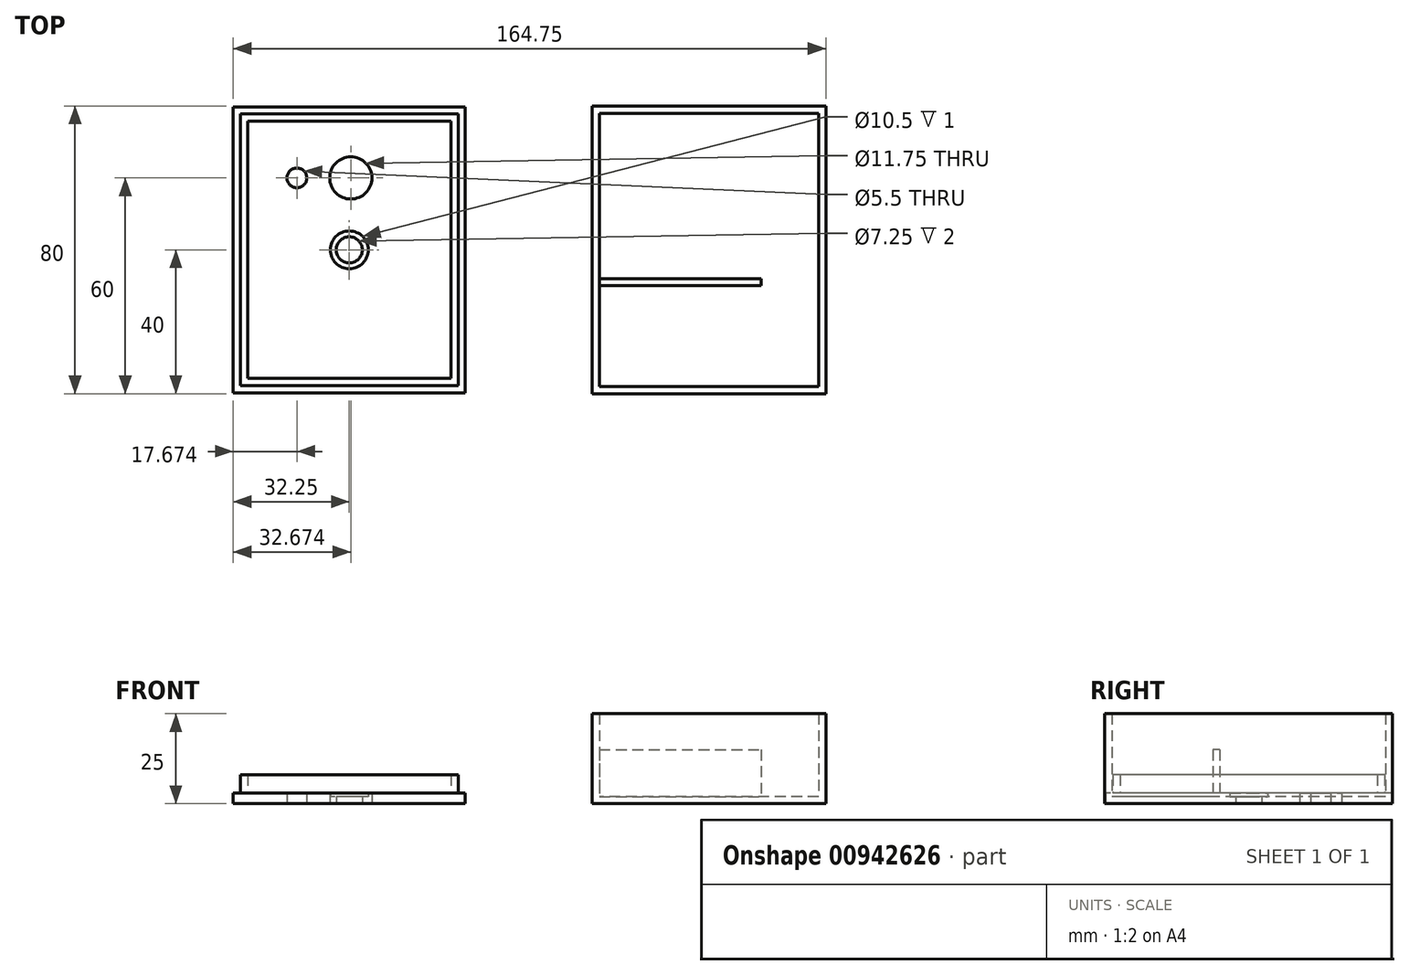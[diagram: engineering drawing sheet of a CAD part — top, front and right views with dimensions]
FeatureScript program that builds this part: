
annotation { "Feature Type Name" : "Feature", "Feature Type Description" : "" }
export const myFeature = defineFeature(function(context is Context, id is Id, definition is map)
    precondition{}
    {
        {
            var Q0;
            Q0=qCreatedBy(makeId("Top.planeOp"),FACE);
            var sketch = newSketch(context, id + "F0", { "sketchPlane" : qUnion([Q0])});
            skLineSegment(sketch, "E0.bottom", {"start": v(32.5, 40) * mm, "end": v(-32.5, 40) * mm});
            skLineSegment(sketch, "E0.top", {"start": v(32.5, -40) * mm, "end": v(-32.5, -40) * mm});
            skLineSegment(sketch, "E0.left", {"start": v(32.5, 40) * mm, "end": v(32.5, -40) * mm});
            skLineSegment(sketch, "E0.right", {"start": v(-32.5, 40) * mm, "end": v(-32.5, -40) * mm});
            skPoint(sketch, "E0.middle", {"position": v(0, 0) * mm});
            skLineSegment(sketch, "E1.0", {"start": v(30.5, 38) * mm, "end": v(-30.5, 38) * mm});
            skLineSegment(sketch, "E1.1", {"start": v(30.5, 38) * mm, "end": v(30.5, -38) * mm});
            skLineSegment(sketch, "E1.2", {"start": v(30.5, -38) * mm, "end": v(-30.5, -38) * mm});
            skLineSegment(sketch, "E1.3", {"start": v(-30.5, 38) * mm, "end": v(-30.5, -38) * mm});
            skLineSegment(sketch, "E2.bottom", {"start": v(-30.5, -8) * mm, "end": v(14.5, -8) * mm});
            skLineSegment(sketch, "E2.top", {"start": v(-30.5, -10) * mm, "end": v(14.5, -10) * mm});
            skLineSegment(sketch, "E2.left", {"start": v(-30.5, -8) * mm, "end": v(-30.5, -10) * mm});
            skLineSegment(sketch, "E2.right", {"start": v(14.5, -8) * mm, "end": v(14.5, -10) * mm});
            skLineSegment(sketch, "E3.bottom", {"start": v(-132.25, 39.75) * mm, "end": v(-67.75, 39.75) * mm});
            skLineSegment(sketch, "E3.top", {"start": v(-132.25, -39.75) * mm, "end": v(-67.75, -39.75) * mm});
            skLineSegment(sketch, "E3.left", {"start": v(-132.25, 39.75) * mm, "end": v(-132.25, -39.75) * mm});
            skLineSegment(sketch, "E3.right", {"start": v(-67.75, 39.75) * mm, "end": v(-67.75, -39.75) * mm});
            skPoint(sketch, "E3.middle", {"position": v(-100, 0) * mm});
            skLineSegment(sketch, "E4.0", {"start": v(-130.25, 37.75) * mm, "end": v(-69.75, 37.75) * mm});
            skLineSegment(sketch, "E4.1", {"start": v(-130.25, 37.75) * mm, "end": v(-130.25, -37.75) * mm});
            skLineSegment(sketch, "E4.2", {"start": v(-130.25, -37.75) * mm, "end": v(-69.75, -37.75) * mm});
            skLineSegment(sketch, "E4.3", {"start": v(-69.75, 37.75) * mm, "end": v(-69.75, -37.75) * mm});
            skLineSegment(sketch, "E5.0", {"start": v(-128.25, 35.75) * mm, "end": v(-71.75, 35.75) * mm});
            skLineSegment(sketch, "E5.1", {"start": v(-128.25, 35.75) * mm, "end": v(-128.25, -35.75) * mm});
            skLineSegment(sketch, "E5.2", {"start": v(-128.25, -35.75) * mm, "end": v(-71.75, -35.75) * mm});
            skLineSegment(sketch, "E5.3", {"start": v(-71.75, 35.75) * mm, "end": v(-71.75, -35.75) * mm});
            skCircle(sketch, "E6", {"center": v(-99.58, 20) * mm, "radius": 5.88 * mm});
            skCircle(sketch, "E7", {"center": v(-100, 0) * mm, "radius": 3.62 * mm});
            skCircle(sketch, "E8", {"center": v(-100, 0) * mm, "radius": 5.25 * mm});
            skCircle(sketch, "E9", {"center": v(-114.58, 20) * mm, "radius": 2.75 * mm});
            skSolve(sketch);
        }
        {
            var Q0;
            {var subQ1=sQuery(id+"F0.wireOp",EDGE,"E1.0");Q0=makeQuery(id+"F0.imprint","IMPRINT",FACE,{"disambiguationData":[TD([[makeQuery(id+"F0.imprint","IMPRINT",EDGE,{"derivedFrom":subQ1}),1.0]])]});}
            extrude(context, id + "F1", {"entities" : qUnion([Q0]), "depth" : 2 * mm, "offsetDistance" : 25 * mm});
        }
        {
            var Q0;
            Q0=makeQuery(id+"F0.imprint","IMPRINT",FACE,{"disambiguationData":[TD([[makeQuery(id+"F0.imprint","IMPRINT",EDGE,{"derivedFrom":sQuery(id+"F0.wireOp",EDGE,"E0.bottom")}),1.0]])]});
            extrude(context, id + "F2", {"entities" : qUnion([Q0]), "operationType" : NewBodyOperationType.ADD, "depth" : 25 * mm, "offsetDistance" : 25 * mm});
        }
        {
            var Q0;
            Q0=makeQuery(id+"F0.imprint","IMPRINT",FACE,{"disambiguationData":[TD([[makeQuery(id+"F0.imprint","IMPRINT",EDGE,{"derivedFrom":sQuery(id+"F0.wireOp",EDGE,"E2.bottom")}),-1.0]])]});
            extrude(context, id + "F3", {"entities" : qUnion([Q0]), "operationType" : NewBodyOperationType.ADD, "depth" : 15 * mm, "offsetDistance" : 25 * mm});
        }
        {
            var Q0;
            Q0=makeQuery(id+"F0.imprint","IMPRINT",FACE,{"disambiguationData":[TD([[makeQuery(id+"F0.imprint","IMPRINT",EDGE,{"derivedFrom":sQuery(id+"F0.wireOp",EDGE,"E3.bottom")}),-1.0]])]});
            var Q1;
            Q1=makeQuery(id+"F0.imprint","IMPRINT",FACE,{"disambiguationData":[TD([[makeQuery(id+"F0.imprint","IMPRINT",EDGE,{"derivedFrom":sQuery(id+"F0.wireOp",EDGE,"E5.0")}),-1.0]])]});
            extrude(context, id + "F4", {"entities" : qUnion([Q0, Q1]), "depth" : 3 * mm, "offsetDistance" : 25 * mm});
        }
        {
            var Q0;
            Q0=makeQuery(id+"F0.imprint","IMPRINT",FACE,{"disambiguationData":[TD([[makeQuery(id+"F0.imprint","IMPRINT",EDGE,{"derivedFrom":sQuery(id+"F0.wireOp",EDGE,"E4.0")}),-1.0]])]});
            extrude(context, id + "F5", {"entities" : qUnion([Q0]), "operationType" : NewBodyOperationType.ADD, "depth" : 8 * mm, "offsetDistance" : 25 * mm});
        }
        {
            var Q0;
            Q0=makeQuery(id+"F0.imprint","IMPRINT",FACE,{"disambiguationData":[TD([[makeQuery(id+"F0.imprint","IMPRINT",EDGE,{"derivedFrom":sQuery(id+"F0.wireOp",EDGE,"E7")}),-1.0]])]});
            extrude(context, id + "F6", {"entities" : qUnion([Q0]), "operationType" : NewBodyOperationType.ADD, "depth" : 2 * mm, "offsetDistance" : 25 * mm});
        }
    });
